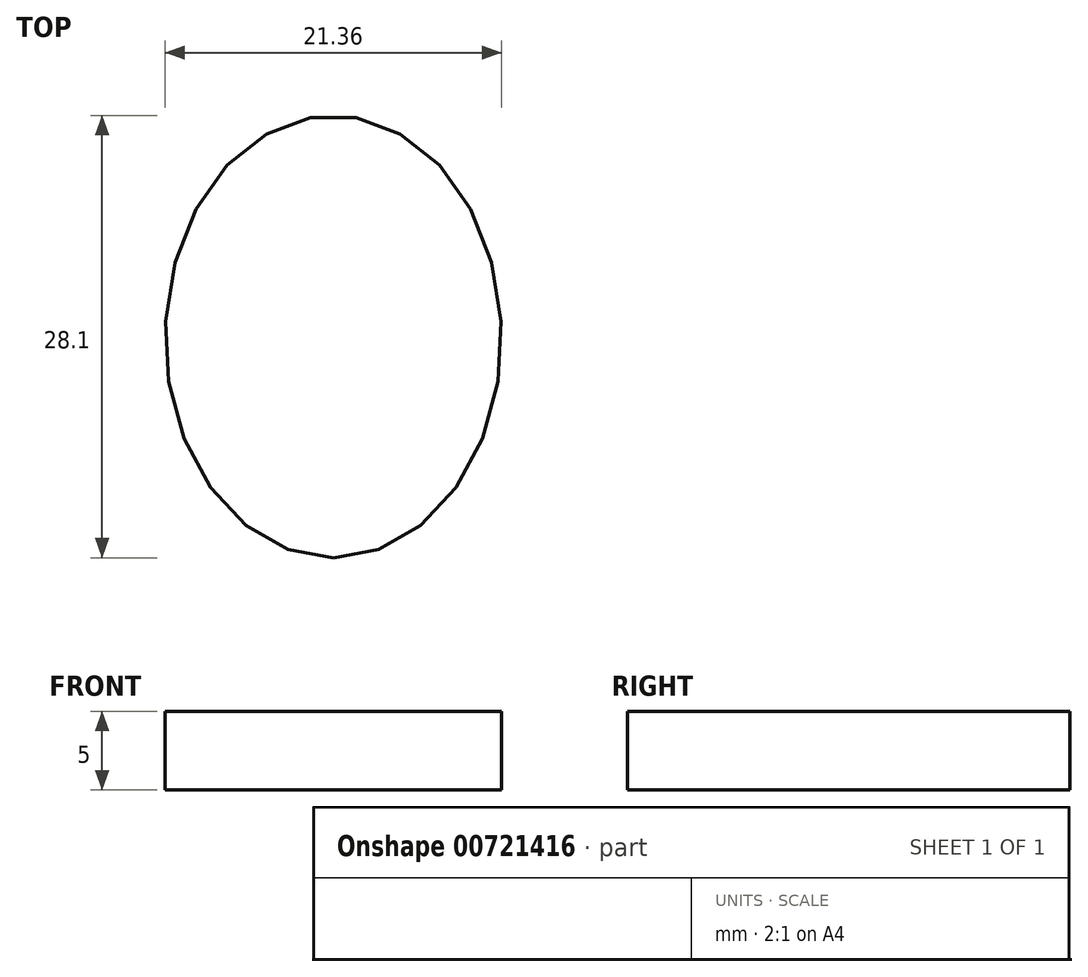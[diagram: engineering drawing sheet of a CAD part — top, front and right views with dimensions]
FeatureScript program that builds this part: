
annotation { "Feature Type Name" : "Feature", "Feature Type Description" : "" }
export const myFeature = defineFeature(function(context is Context, id is Id, definition is map)
    precondition{}
    {
        {
            var Q0;
            Q0=qCreatedBy(makeId("Top.planeOp"),FACE);
            var sketch = newSketch(context, id + "F0", { "sketchPlane" : qUnion([Q0])});
            skEllipse(sketch, "E0", {"center": v(0, 0) * mm, "majorRadius": 14.05 * mm, "minorRadius": 10.68 * mm, "majorAxis": v(0, -1)});
            skSolve(sketch);
        }
        {
            var Q0;
            Q0 = qSketchRegion(id + "F0", true);
            extrude(context, id + "F1", {"entities" : qUnion([Q0]), "depth" : 5 * mm, "offsetDistance" : 25 * mm});
        }
    });
